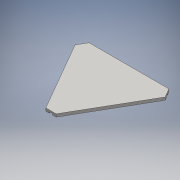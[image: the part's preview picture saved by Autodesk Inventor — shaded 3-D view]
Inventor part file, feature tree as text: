
AUTODESK INVENTOR PART (.ipt)
format: ipt  version: 2016 SP1 (Build 200210100, 210)  size: 142,336 bytes
history: native  units: mm
features: reference x3, extrude x2, sketch x2, projected_geometry x1
ambient origin geometry x8: Origin, YZ Plane, XZ Plane, XY Plane, X Axis, Y Axis, Z Axis, Center Point
bodies: Solid1 (feature_tree)
feature tree (8):
  extrude  "Extrusion1"  Depth=20.0mm
  extrude  "Extrusion2"  [1 undecoded]
  sketch  "Sketch1"  dims[d0=18.0mm d1=0.0mm d2=20.0mm]
  reference  "Reference1"
  reference  "Reference2"
  reference  "Reference3"
  sketch  "Sketch2"  dims[d3=8.0mm d4=0.0mm]
  projected_geometry  "Projected Loop1"
note: 1 required parameter value undecoded (feature->parameter linkage not recoverable at this tier; creation-order binding heuristic only, values carry confidence <= 0.55)
